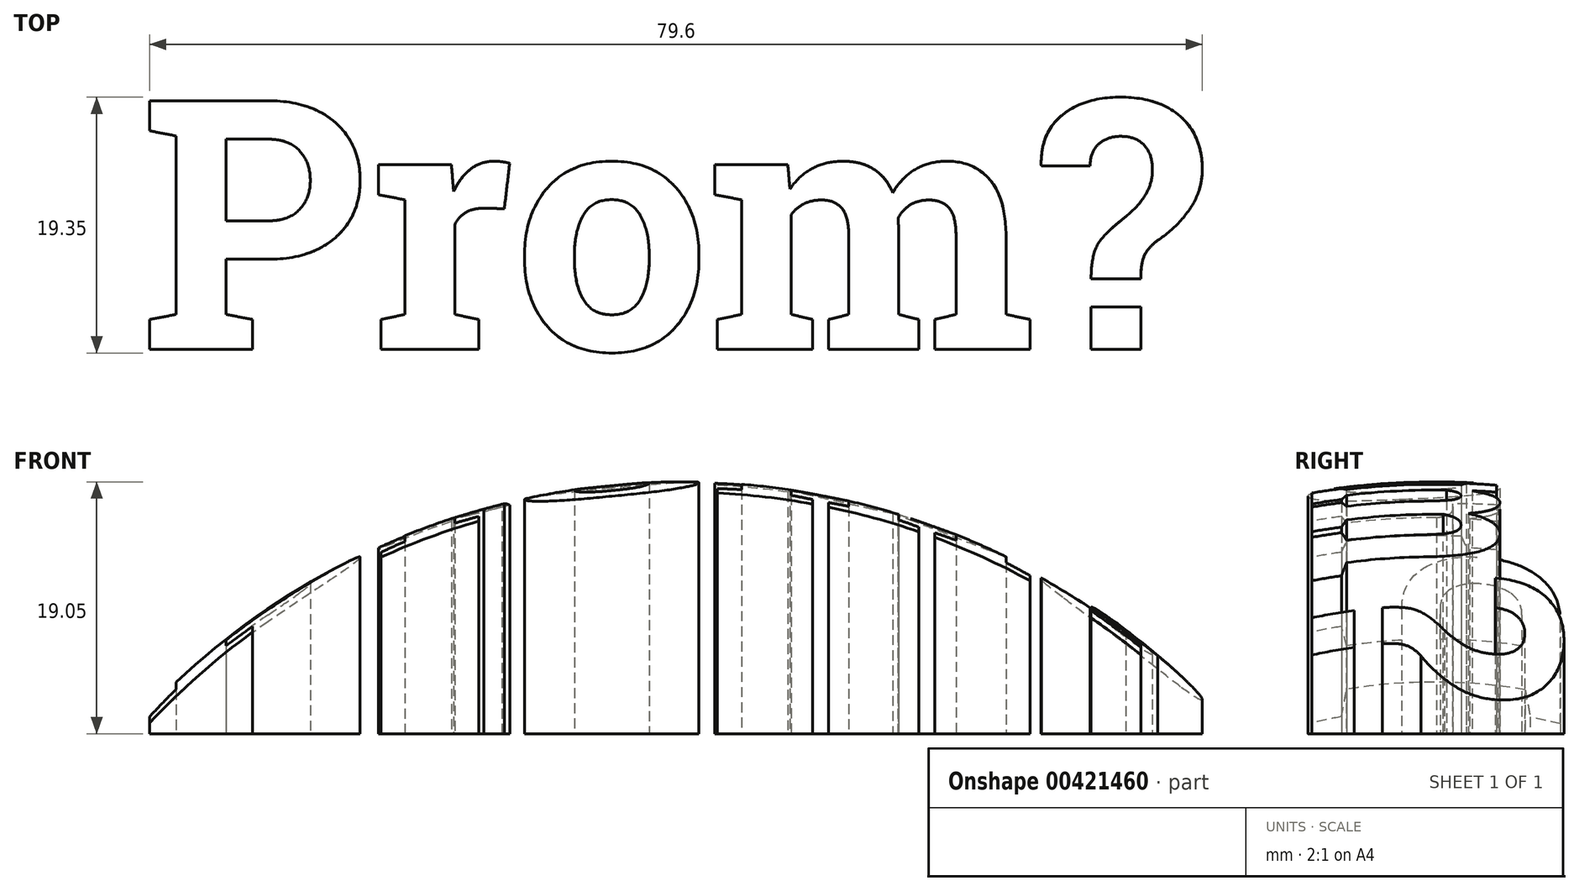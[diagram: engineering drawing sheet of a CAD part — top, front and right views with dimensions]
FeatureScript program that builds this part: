
annotation { "Feature Type Name" : "Feature", "Feature Type Description" : "" }
export const myFeature = defineFeature(function(context is Context, id is Id, definition is map)
    precondition{}
    {
        {
            var Q0;
            Q0=qCreatedBy(makeId("Top.planeOp"),FACE);
            var sketch = newSketch(context, id + "F0", { "sketchPlane" : qUnion([Q0])});
            skText(sketch, "E0", { "text": "Prom?", "fontName": "RobotoSlab-Bold.ttf"});
            const initialGuessF0  = {"E0": [-0.04097, -0.00929, 1, 0, 0.01905]};
            skSetInitialGuess(sketch, initialGuessF0);
            skSolve(sketch);
        }
        {
            var Q0;
            Q0 = qSketchRegion(id + "F0", true);
            extrude(context, id + "F1", {"entities" : qUnion([Q0]), "depth" : 19.05 * mm});
        }
        {
            var Q0;
            Q0=qCreatedBy(makeId("Front.planeOp"),FACE);
            var sketch = newSketch(context, id + "F2", { "sketchPlane" : qUnion([Q0])});
            skLineSegment(sketch, "E1", {"start": v(0, 0) * mm, "end": v(0, 19.05) * mm});
            skLineSegment(sketch, "E2", {"start": v(0, 19.05) * mm, "end": v(0, -36.83) * mm});
            skPoint(sketch, "E2.endSnap0", {"position": v(0, 9.53) * mm});
            skCircle(sketch, "E3", {"center": v(0, -36.83) * mm, "radius": 55.88 * mm});
            skCircle(sketch, "E4", {"center": v(0, -36.83) * mm, "radius": 76.2 * mm});
            skLineSegment(sketch, "E5", {"start": v(0, -36.83) * mm, "end": v(76.2, -36.83) * mm});
            skLineSegment(sketch, "E6", {"start": v(0, -36.83) * mm, "end": v(-76.2, -36.83) * mm});
            skSolve(sketch);
        }
        {
            var Q0;
            {var subQ5=sQuery(id+"F2.wireOp",EDGE,"E3");var subQ7=makeQuery(id+"F2.imprint","INTERSECT",VERTEX,{"derivedFrom":[sQuery(id+"F2.wireOp",EDGE,"E2"),subQ5]});Q0=makeQuery(id+"F2.imprint","IMPRINT",FACE,{"disambiguationData":[TD([[makeQuery(id+"F2.imprint","IMPRINT",EDGE,{"disambiguationData":[TD([[subQ7,1.0]])],"derivedFrom":subQ5}),-1.0]])]});}
            var Q1;
            Q1=sQuery(id+"F2.wireOp",EDGE,"E6");
            revolve(context, id + "F3", {"operationType" : NewBodyOperationType.REMOVE, "entities" : qUnion([Q0]), "axis" : qUnion([Q1]), "revolveType" : RevolveType.FULL, "oppositeDirection" : true});
        }
    });
